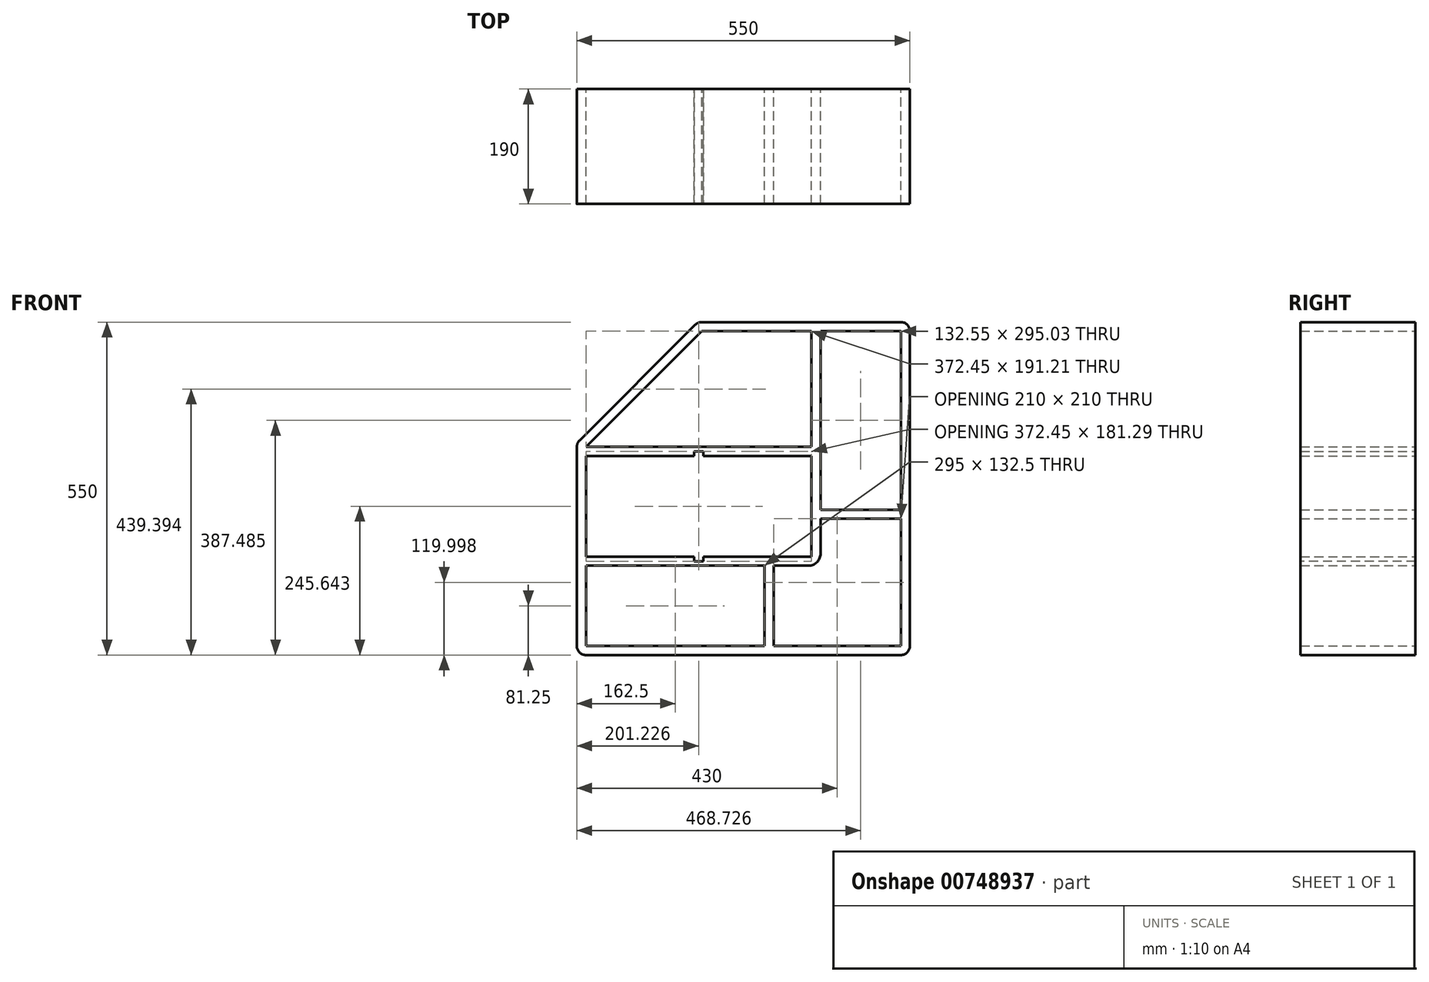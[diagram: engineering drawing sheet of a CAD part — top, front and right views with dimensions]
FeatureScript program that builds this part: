
annotation { "Feature Type Name" : "Feature", "Feature Type Description" : "" }
export const myFeature = defineFeature(function(context is Context, id is Id, definition is map)
    precondition{}
    {
        {
            var Q0;
            Q0=qCreatedBy(makeId("Front.planeOp"),FACE);
            var sketch = newSketch(context, id + "F0", { "sketchPlane" : qUnion([Q0])});
            skLineSegment(sketch, "E0.bottom", {"start": v(-68.83, 275) * mm, "end": v(260, 275) * mm});
            skLineSegment(sketch, "E0.top", {"start": v(-260, -275) * mm, "end": v(260, -275) * mm});
            skLineSegment(sketch, "E0.left", {"start": v(-275, 68.79) * mm, "end": v(-275, -260) * mm});
            skLineSegment(sketch, "E0.right", {"start": v(275, 260) * mm, "end": v(275, -260) * mm});
            skPoint(sketch, "E0.middle", {"position": v(0, 0) * mm});
            skLineSegment(sketch, "E1.bottom", {"start": v(-275, -275) * mm, "end": v(-375, -275) * mm, "construction": true});
            skLineSegment(sketch, "E1.top", {"start": v(-275, 75) * mm, "end": v(-375, 75) * mm, "construction": true});
            skLineSegment(sketch, "E1.right", {"start": v(-375, -275) * mm, "end": v(-375, 75) * mm, "construction": true});
            skLineSegment(sketch, "E2.MirrorCS", {"start": v(274.96, 375) * mm, "end": v(-75.04, 375) * mm, "construction": true});
            skLineSegment(sketch, "E3.MirrorCS", {"start": v(274.96, 275) * mm, "end": v(274.96, 375) * mm, "construction": true});
            skLineSegment(sketch, "E4.MirrorCS", {"start": v(-75.04, 275) * mm, "end": v(-75.04, 375) * mm, "construction": true});
            skLineSegment(sketch, "E5", {"start": v(-270.6, 79.4) * mm, "end": v(-79.44, 270.6) * mm});
            skLineSegment(sketch, "E6.0", {"start": v(-68.83, 260) * mm, "end": v(112.45, 260) * mm});
            skLineSegment(sketch, "E6.1", {"start": v(-260, 68.79) * mm, "end": v(-68.83, 260) * mm});
            skLineSegment(sketch, "E6.2", {"start": v(260, 260) * mm, "end": v(260, -35) * mm});
            skLineSegment(sketch, "E6.3", {"start": v(-260, -260) * mm, "end": v(35, -260) * mm});
            skLineSegment(sketch, "E6.4", {"start": v(-260, -127.5) * mm, "end": v(-260, -260) * mm});
            skLineSegment(sketch, "E7", {"start": v(260, -260) * mm, "end": v(50, -260) * mm, "construction": true});
            skLineSegment(sketch, "E8", {"start": v(35, -260) * mm, "end": v(35, -267.5) * mm});
            skLineSegment(sketch, "E9", {"start": v(50, -267.5) * mm, "end": v(50, -260) * mm});
            skLineSegment(sketch, "E10.trimOffspring", {"start": v(50, -260) * mm, "end": v(260, -260) * mm});
            skLineSegment(sketch, "E11.bottom", {"start": v(50, -267.5) * mm, "end": v(35, -267.5) * mm});
            skLineSegment(sketch, "E11.left", {"start": v(50, -267.5) * mm, "end": v(50, -127.5) * mm});
            skLineSegment(sketch, "E11.right", {"start": v(35, -267.5) * mm, "end": v(35, -127.5) * mm});
            skLineSegment(sketch, "E12", {"start": v(50, -127.5) * mm, "end": v(107.45, -127.5) * mm});
            skLineSegment(sketch, "E13.trimOffspring", {"start": v(112.45, -112.5) * mm, "end": v(-66.27, -112.5) * mm});
            skLineSegment(sketch, "E14", {"start": v(112.45, -112.5) * mm, "end": v(112.45, 53.79) * mm});
            skLineSegment(sketch, "E15", {"start": v(127.45, -107.5) * mm, "end": v(127.45, -50.03) * mm});
            skLineSegment(sketch, "E16", {"start": v(35, -127.5) * mm, "end": v(35, -120) * mm});
            skLineSegment(sketch, "E17", {"start": v(35, -120) * mm, "end": v(50, -120.05) * mm});
            skLineSegment(sketch, "E18", {"start": v(50, -127.5) * mm, "end": v(50, -120.05) * mm});
            skLineSegment(sketch, "E19", {"start": v(-260, 68.79) * mm, "end": v(-100, 68.79) * mm});
            skLineSegment(sketch, "E20", {"start": v(-260, -112.5) * mm, "end": v(-260, 53.79) * mm});
            skLineSegment(sketch, "E21", {"start": v(275, -275) * mm, "end": v(-224.92, 224.82) * mm, "construction": true});
            skLineSegment(sketch, "E22.MirrorCS", {"start": v(267.45, -50) * mm, "end": v(267.45, -35) * mm});
            skLineSegment(sketch, "E23.MirrorCS", {"start": v(267.45, -50) * mm, "end": v(127.45, -50.03) * mm});
            skLineSegment(sketch, "E24.MirrorCS", {"start": v(127.45, -50.03) * mm, "end": v(120, -50.03) * mm});
            skLineSegment(sketch, "E25.MirrorCS", {"start": v(119.95, -35.03) * mm, "end": v(120, -50.03) * mm});
            skLineSegment(sketch, "E26.MirrorCS", {"start": v(127.45, -35.03) * mm, "end": v(119.95, -35.03) * mm});
            skLineSegment(sketch, "E27.MirrorCS", {"start": v(267.45, -35) * mm, "end": v(127.45, -35.03) * mm});
            skLineSegment(sketch, "E28.trimOffspring", {"start": v(127.45, -35.03) * mm, "end": v(127.45, 260) * mm});
            skLineSegment(sketch, "E29.trimOffspring", {"start": v(260, -50) * mm, "end": v(260, -260) * mm});
            skLineSegment(sketch, "E30", {"start": v(35, -127.5) * mm, "end": v(-260, -127.5) * mm});
            skLineSegment(sketch, "E31", {"start": v(-260, -127.5) * mm, "end": v(-267.5, -127.5) * mm});
            skLineSegment(sketch, "E32", {"start": v(-267.5, -127.5) * mm, "end": v(-267.5, -112.5) * mm});
            skLineSegment(sketch, "E33", {"start": v(-267.5, -112.5) * mm, "end": v(-260, -112.5) * mm});
            skLineSegment(sketch, "E34", {"start": v(112.45, 260) * mm, "end": v(112.45, 267.5) * mm});
            skLineSegment(sketch, "E35", {"start": v(112.45, 267.5) * mm, "end": v(127.45, 267.5) * mm});
            skLineSegment(sketch, "E36", {"start": v(127.45, 267.5) * mm, "end": v(127.45, 260) * mm});
            skLineSegment(sketch, "E37.trimOffspring", {"start": v(127.45, 260) * mm, "end": v(260, 260) * mm});
            skLineSegment(sketch, "E38.trimOffspring", {"start": v(-47.55, 68.79) * mm, "end": v(112.45, 68.79) * mm});
            skPoint(sketch, "E39.visualSharp", {"position": v(-75.04, 275) * mm});
            skArc(sketch, "E39.filletArc", {"start": v(-68.83, 275) * mm, "mid": v(-74.57, 273.86) * mm, "end": v(-79.44, 270.6) * mm});
            skPoint(sketch, "E40.visualSharp", {"position": v(-275, 75) * mm});
            skArc(sketch, "E40.filletArc", {"start": v(-270.6, 79.4) * mm, "mid": v(-273.86, 74.53) * mm, "end": v(-275, 68.79) * mm});
            skPoint(sketch, "E41.visualSharp", {"position": v(275, 275) * mm});
            skArc(sketch, "E41.filletArc", {"start": v(275, 260) * mm, "mid": v(270.6, 270.6) * mm, "end": v(260, 275) * mm});
            skPoint(sketch, "E42.visualSharp", {"position": v(275, -275) * mm});
            skArc(sketch, "E42.filletArc", {"start": v(260, -275) * mm, "mid": v(270.6, -270.6) * mm, "end": v(275, -260) * mm});
            skPoint(sketch, "E43.visualSharp", {"position": v(-275, -275) * mm});
            skArc(sketch, "E43.filletArc", {"start": v(-275, -260) * mm, "mid": v(-270.6, -270.6) * mm, "end": v(-260, -275) * mm});
            skPoint(sketch, "E44.visualSharp", {"position": v(127.45, -127.5) * mm});
            skArc(sketch, "E44.filletArc", {"start": v(107.45, -127.5) * mm, "mid": v(121.6, -121.64) * mm, "end": v(127.45, -107.5) * mm});
            skLineSegment(sketch, "E45", {"start": v(21.81, 260) * mm, "end": v(21.81, 220) * mm});
            skLineSegment(sketch, "E46", {"start": v(112.45, 220) * mm, "end": v(-108.82, 220) * mm});
            skLineSegment(sketch, "E47", {"start": v(-100, 68.79) * mm, "end": v(-47.55, 68.79) * mm});
            skLineSegment(sketch, "E48.0", {"start": v(-47.55, 53.79) * mm, "end": v(112.45, 53.79) * mm});
            skLineSegment(sketch, "E48.1", {"start": v(-100, 53.79) * mm, "end": v(-81.27, 53.79) * mm});
            skLineSegment(sketch, "E48.2", {"start": v(-260, 53.79) * mm, "end": v(-100, 53.79) * mm});
            skLineSegment(sketch, "E49.trimOffspring", {"start": v(112.45, 68.79) * mm, "end": v(112.45, 260) * mm});
            skCircle(sketch, "E50", {"center": v(-166.89, -29.36) * mm, "radius": 65 * mm});
            skCircle(sketch, "E51", {"center": v(19.34, -29.36) * mm, "radius": 65 * mm});
            skLineSegment(sketch, "E52", {"start": v(-260, 53.79) * mm, "end": v(-267.5, 53.79) * mm});
            skLineSegment(sketch, "E53", {"start": v(-267.5, 53.79) * mm, "end": v(-267.5, 68.79) * mm});
            skLineSegment(sketch, "E54", {"start": v(-267.5, 68.79) * mm, "end": v(-260, 68.79) * mm});
            skLineSegment(sketch, "E55", {"start": v(112.45, 53.79) * mm, "end": v(119.95, 53.79) * mm});
            skLineSegment(sketch, "E56", {"start": v(119.95, 53.79) * mm, "end": v(119.95, 68.79) * mm});
            skLineSegment(sketch, "E57", {"start": v(119.95, 68.79) * mm, "end": v(112.45, 68.79) * mm});
            skLineSegment(sketch, "E58", {"start": v(-73.77, -120) * mm, "end": v(-66.27, -120) * mm});
            skLineSegment(sketch, "E59", {"start": v(-66.27, -120) * mm, "end": v(-66.27, -112.5) * mm});
            skLineSegment(sketch, "E60", {"start": v(-73.77, -120) * mm, "end": v(-81.27, -120) * mm});
            skLineSegment(sketch, "E61", {"start": v(-81.27, -120) * mm, "end": v(-81.27, -112.5) * mm});
            skLineSegment(sketch, "E62.trimOffspring", {"start": v(-81.27, -112.5) * mm, "end": v(-260, -112.5) * mm});
            skPoint(sketch, "E63.oppositeSnap0", {"position": v(-81.27, -116.25) * mm});
            skLineSegment(sketch, "E63.bottom", {"start": v(-66.27, -120) * mm, "end": v(-81.27, -120) * mm});
            skLineSegment(sketch, "E63.top", {"start": v(-66.27, 68.79) * mm, "end": v(-81.27, 68.79) * mm});
            skLineSegment(sketch, "E63.left", {"start": v(-66.27, -120) * mm, "end": v(-66.27, 53.79) * mm});
            skLineSegment(sketch, "E63.right", {"start": v(-81.27, -120) * mm, "end": v(-81.27, 53.79) * mm});
            skLineSegment(sketch, "E64.trimOffspring", {"start": v(-66.27, 53.79) * mm, "end": v(-47.55, 53.79) * mm});
            skLineSegment(sketch, "E65.top", {"start": v(-81.27, 61.29) * mm, "end": v(-66.27, 61.29) * mm});
            skLineSegment(sketch, "E65.left", {"start": v(-81.27, 53.79) * mm, "end": v(-81.27, 61.29) * mm});
            skLineSegment(sketch, "E65.right", {"start": v(-66.27, 53.79) * mm, "end": v(-66.27, 61.29) * mm});
            skSolve(sketch);
        }
        {
            var Q0;
            Q0 = qSketchRegion(id + "F0", true);
            var Q1;
            {var subQ2=sQuery(id+"F0.wireOp",EDGE,"E63.bottom");Q1=makeQuery(id+"F0.imprint","IMPRINT",FACE,{"disambiguationData":[TD([[makeQuery(id+"F0.imprint","IMPRINT",EDGE,{"derivedFrom":subQ2}),-1.0]])]});}
            var Q2;
            {var subQ0=sQuery(id+"F0.wireOp",EDGE,"E19");Q2=makeQuery(id+"F0.imprint","IMPRINT",FACE,{"disambiguationData":[TD([[makeQuery(id+"F0.imprint","IMPRINT",EDGE,{"derivedFrom":subQ0}),-1.0]])]});}
            var Q3;
            Q3=makeQuery(id+"F0.imprint","IMPRINT",FACE,{"disambiguationData":[TD([[makeQuery(id+"F0.imprint","IMPRINT",EDGE,{"derivedFrom":sQuery(id+"F0.wireOp",EDGE,"E12")}),1.0]])]});
            var Q4;
            {var subQ1=sQuery(id+"F0.wireOp",EDGE,"E11.bottom");Q4=makeQuery(id+"F0.imprint","IMPRINT",FACE,{"disambiguationData":[TD([[makeQuery(id+"F0.imprint","IMPRINT",EDGE,{"derivedFrom":subQ1}),-1.0]])]});}
            var Q5;
            {var subQ3=sQuery(id+"F0.wireOp",EDGE,"E22.MirrorCS");Q5=makeQuery(id+"F0.imprint","IMPRINT",FACE,{"disambiguationData":[TD([[makeQuery(id+"F0.imprint","IMPRINT",EDGE,{"derivedFrom":subQ3}),1.0]])]});}
            extrude(context, id + "F1", {"entities" : qUnion([Q0, Q1, Q2, Q3, Q4, Q5]), "depth" : 190 * mm, "offsetDistance" : 25 * mm});
        }
    });
